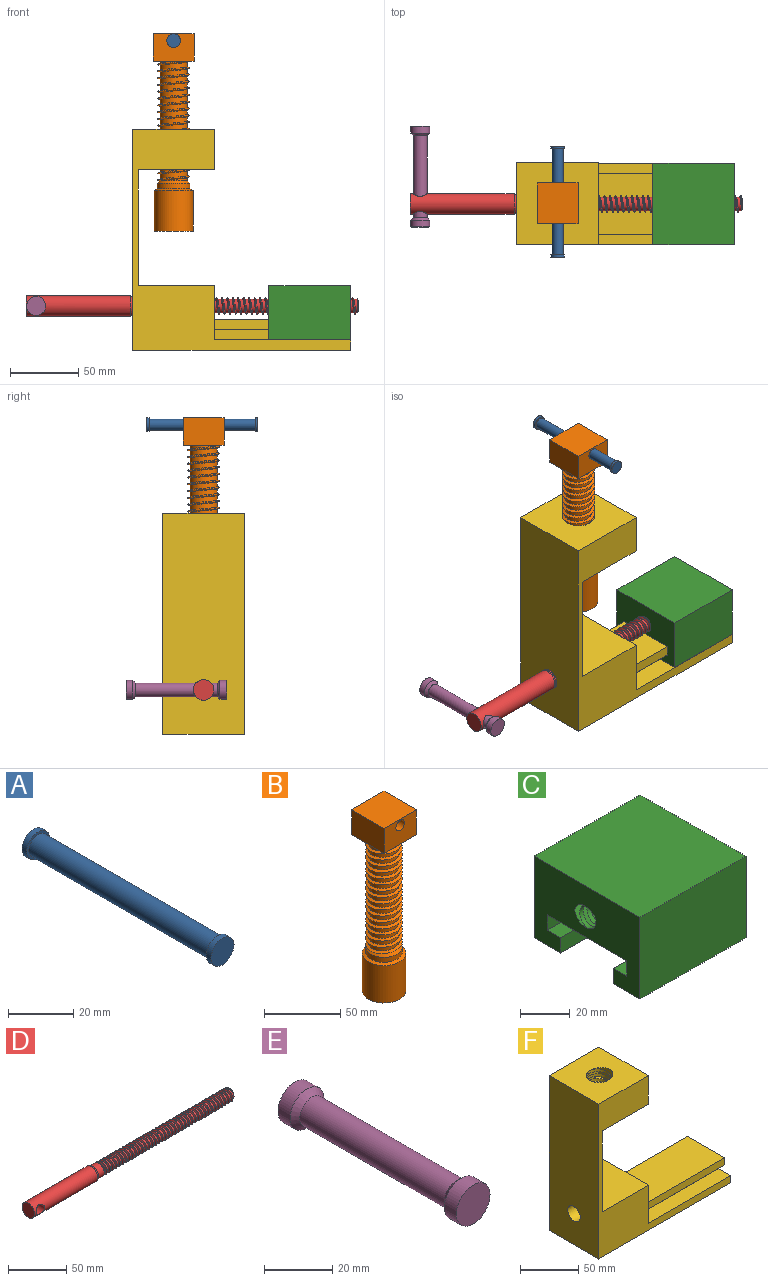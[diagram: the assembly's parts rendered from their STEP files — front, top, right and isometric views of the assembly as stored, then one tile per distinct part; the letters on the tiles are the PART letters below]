
ASSEMBLY  parts=6 mates=5
PART A: 7 faces, bbox 10x82x10 mm
  f0: cylinder r=4mm len=78mm, axis (0,-1,0), area 1960.4mm2, adj f3,f6
  f1: cylinder r=5mm len=10mm, axis (0,1,0), area 62.8mm2, adj f2,f3
  f2: plane 10x10mm, normal (0,-1,0), area 78.5mm2, adj f1
  f3: plane 10x10mm, normal (0,1,0), area 28.3mm2, adj f0,f1
  f4: cylinder r=5mm len=10mm, axis (0,-1,0), area 62.8mm2, adj f5,f6
  f5: plane 10x10mm, normal (0,1,0), area 78.5mm2, adj f4
  f6: plane 10x10mm, normal (0,-1,0), area 28.3mm2, adj f0,f4
PART B: 15 faces, bbox 30.4x30.4x145.4 mm
  f0: bspline ~91.58x27.71mm, area 2636.6mm2, adj f1,f2,f3,f11
  f1: bspline ~91.58x27.71mm, area 2631mm2, adj f0,f2,f3,f11
  f2: cylinder r=10mm len=88mm, axis (0,0,-1), area 4649.1mm2, adj f0,f1,f3,f11
  f3: plane 30.44x30.44mm, normal (0,0,-1), area 565.7mm2, adj f0,f1,f2,f4,f5,f6,f7
  f4: plane 30x20mm, normal (0,-1,0), area 549.7mm2, adj f3,f5,f7,f8,f9
  f5: plane 30x20mm, normal (1,0,0), area 600mm2, adj f3,f4,f6,f8
  f6: plane 30x20mm, normal (0,1,0), area 549.7mm2, adj f3,f5,f7,f8,f9
  f7: plane 30x20mm, normal (-1,0,0), area 600mm2, adj f3,f4,f6,f8
  f8: plane 30x30mm, normal (0,0,1), area 900mm2, adj f4,f5,f6,f7
  f9: cylinder r=4mm len=30mm, axis (0,-1,0), area 754mm2, adj f4,f6
  f10: cylinder r=12mm len=24mm, axis (0,0,-1), area 301.6mm2, adj f11,f14
  f11: cone r=10mm half-angle=45deg, axis (0,0,-1), area 167mm2, adj f0,f1,f2,f10
  f12: plane 28.57x28.57mm, normal (0,0,-1), area 641.1mm2, adj f13
  f13: cylinder r=14.28mm len=30mm, axis (0,0,-1), area 2692.6mm2, adj f12,f14
  f14: cone r=12mm half-angle=66.4deg, axis (0,0,-1), area 206mm2, adj f10,f13
PART C: 15 faces, bbox 60x60x40 mm
  f0: plane 60x40mm, normal (1,0,0), area 1742mm2, adj f2,f3,f4,f5,f6,f7,f8,f9
  f1: plane 60x40mm, normal (-1,0,0), area 1742mm2, adj f2,f3,f4,f5,f6,f7,f8,f9
  f2: plane 60x15mm, normal (0,0,-1), area 900mm2, adj f0,f1,f3,f13
  f3: plane 60x40mm, normal (0,1,0), area 2400mm2, adj f0,f1,f2,f6
  f4: plane 60x40mm, normal (0,-1,0), area 2400mm2, adj f0,f1,f5,f6
  f5: plane 60x15mm, normal (0,0,-1), area 900mm2, adj f0,f1,f4,f7
  f6: plane 60x60mm, normal (0,0,1), area 3600mm2, adj f0,f1,f3,f4
  f7: plane 60x7.5mm, normal (0,1,0), area 450mm2, adj f0,f1,f5,f8
  f8: plane 60x7.5mm, normal (0,0,1), area 450mm2, adj f0,f1,f7,f9
  f9: plane 60x7.5mm, normal (0,1,0), area 450mm2, adj f0,f1,f8,f10
  f10: plane 60x45mm, normal (0,0,-1), area 2700mm2, adj f0,f1,f9,f11
  f11: plane 60x7.5mm, normal (0,-1,0), area 450mm2, adj f0,f1,f10,f12
  f12: plane 60x7.5mm, normal (0,0,1), area 450mm2, adj f0,f1,f11,f13
  f13: plane 60x7.5mm, normal (0,-1,0), area 450mm2, adj f0,f1,f2,f12
  f14: cylinder r=5mm len=60mm, axis (-1,0,0), area 956.5mm2, adj f0,f1
PART D: 11 faces, bbox 244.6x15x15 mm
  f0: cylinder r=7.5mm len=76.5mm, axis (1,0,0), area 3429.9mm2, adj f8,f9,f10
  f1: bspline ~158.37x13mm, area 2364.5mm2, adj f2,f3,f4,f6
  f2: bspline ~159.86x12.99mm, area 2397mm2, adj f1,f3,f4,f6
  f3: cylinder r=5mm len=156.87mm, axis (-1,0,0), area -96.5mm2, adj f1,f2,f4,f6
  f4: torus R=4mm, axis (-1,0,0), area 38.6mm2, adj f1,f2,f3,f5
  f5: plane 8x8mm, normal (1,0,0), area 50.3mm2, adj f4
  f6: cone r=5mm half-angle=45deg, axis (-1,0,0), area 62.6mm2, adj f1,f2,f3,f7
  f7: cylinder r=6.5mm len=13mm, axis (1,0,0), area 285.9mm2, adj f6,f8
  f8: cone r=6.5mm half-angle=26.6deg, axis (-1,0,0), area 98.3mm2, adj f0,f7
  f9: plane 15x15mm, normal (-1,0,0), area 176.7mm2, adj f0
  f10: cylinder r=5.1mm len=11mm, axis (0,1,0), area 352.4mm2, adj f0
PART E: 7 faces, bbox 14x74x14 mm
  f0: cylinder r=5mm len=60mm, axis (0,1,0), area 1885mm2, adj f1,f4
  f1: cone r=5mm half-angle=45deg, axis (0,1,0), area 106.6mm2, adj f0,f2
  f2: cylinder r=7mm len=14mm, axis (0,-1,0), area 219.9mm2, adj f1,f3
  f3: plane 14x14mm, normal (0,1,0), area 153.9mm2, adj f2
  f4: cone r=5mm half-angle=45deg, axis (0,-1,0), area 106.6mm2, adj f0,f5
  f5: cylinder r=7mm len=14mm, axis (0,1,0), area 219.9mm2, adj f4,f6
  f6: plane 14x14mm, normal (0,-1,0), area 153.9mm2, adj f5
PART F: 22 faces, bbox 160x60x162.5 mm
  f0: plane 60x56mm, normal (0,0,-1), area 2967.2mm2, adj f2,f4,f5,f6,f20
  f1: plane 60x60mm, normal (0,0,1), area 3207.2mm2, adj f2,f3,f4,f5,f6
  f2: plane 162.5x160mm, normal (0,1,0), area 5740mm2, adj f0,f1,f3,f5,f7,f8,f10,f11
  f3: plane 162.5x60mm, normal (-1,0,0), area 9568.5mm2, adj f1,f2,f4,f12,f21
  f4: plane 162.5x160mm, normal (0,-1,0), area 5740mm2, adj f0,f1,f3,f5,f7,f8,f9,f11
  f5: plane 60x30mm, normal (1,0,0), area 1800mm2, adj f0,f1,f2,f4
  f6: cylinder r=10.5mm len=30mm, axis (0,0,-1), area 1097.9mm2, adj f0,f1
  f7: plane 60x56mm, normal (0,0,1), area 3360mm2, adj f2,f4,f8,f20
  f8: plane 60x40mm, normal (1,0,0), area 1656mm2, adj f2,f4,f7,f9,f10,f13,f14,f15
  f9: plane 100x15mm, normal (0,0,1), area 1500mm2, adj f4,f8,f11,f13
  f10: plane 100x15mm, normal (0,0,1), area 1500mm2, adj f2,f8,f11,f19
  f11: plane 60x22.5mm, normal (1,0,0), area 1012.5mm2, adj f2,f4,f9,f10,f12,f13,f14,f15
  f12: plane 160x60mm, normal (0,0,-1), area 9600mm2, adj f2,f3,f4,f11
  f13: plane 100x7.5mm, normal (0,-1,0), area 750mm2, adj f8,f9,f11,f14
  f14: plane 100x7.5mm, normal (0,0,-1), area 750mm2, adj f8,f11,f13,f15
  f15: plane 100x7.5mm, normal (0,-1,0), area 750mm2, adj f8,f11,f14,f16
  f16: plane 100x45mm, normal (0,0,1), area 4500mm2, adj f8,f11,f15,f17
  f17: plane 100x7.5mm, normal (0,1,0), area 750mm2, adj f8,f11,f16,f18
  f18: plane 100x7.5mm, normal (0,0,-1), area 750mm2, adj f8,f11,f17,f19
  f19: plane 100x7.5mm, normal (0,1,0), area 750mm2, adj f8,f10,f11,f18
  f20: plane 85x60mm, normal (1,0,0), area 5100mm2, adj f0,f2,f4,f7
  f21: cylinder r=7.6mm len=60mm, axis (1,0,0), area 2865.1mm2, adj f3,f8
PLACE A rot(axis=(0,0,-1),0deg) t=(0,1.09,40)mm
PLACE B rot(axis=(-0.01,0,-1),0deg) t=(0,0,40)mm
PLACE C at identity
PLACE D t=(-63.5,0,0)mm
PLACE E t=(-63.5,20,0)mm
PLACE F at identity fixed
MATE revolute D.f6 <-> F.f21  axis (1,0,0) through (-30,0,-100)mm
MATE slider E.f0 <-> D.f10  axis (0,1,0) through (-101,20,-100)mm
MATE slider C.f0 <-> F.f11  axis (1,0,0) through (130,0,-110)mm
MATE cylindrical F.f6 <-> B.f10  axis (0,0,-1) through (0,0,-85)mm
MATE slider A.f0 <-> B.f9  axis (0,-1,0) through (0,1.09,95)mm
